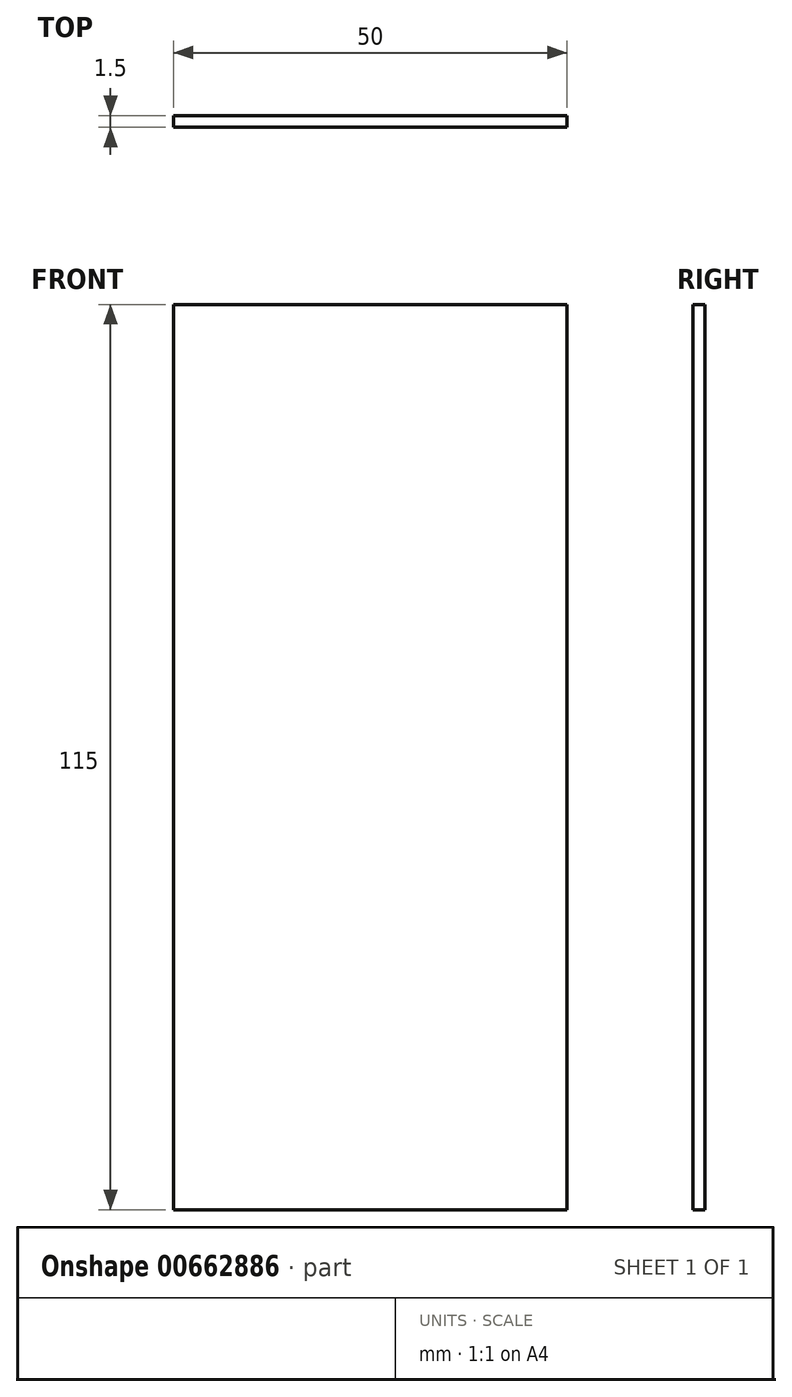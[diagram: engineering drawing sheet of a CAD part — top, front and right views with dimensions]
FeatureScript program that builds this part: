
annotation { "Feature Type Name" : "Feature", "Feature Type Description" : "" }
export const myFeature = defineFeature(function(context is Context, id is Id, definition is map)
    precondition{}
    {
        {
            var Q0;
            Q0=qCreatedBy(makeId("Front.planeOp"),FACE);
            var sketch = newSketch(context, id + "F0", { "sketchPlane" : qUnion([Q0])});
            skLineSegment(sketch, "E0.bottom", {"start": v(0, 57.5) * mm, "end": v(-50, 57.5) * mm});
            skLineSegment(sketch, "E0.top", {"start": v(0, -57.5) * mm, "end": v(-50, -57.5) * mm});
            skLineSegment(sketch, "E0.left", {"start": v(0, 57.5) * mm, "end": v(0, -57.5) * mm});
            skLineSegment(sketch, "E0.right", {"start": v(-50, 57.5) * mm, "end": v(-50, -57.5) * mm});
            skSolve(sketch);
        }
        {
            var Q0;
            Q0 = qSketchRegion(id + "F0", true);
            extrude(context, id + "F1", {"entities" : qUnion([Q0]), "depth" : 1.5 * mm, "offsetDistance" : 25 * mm});
        }
    });
